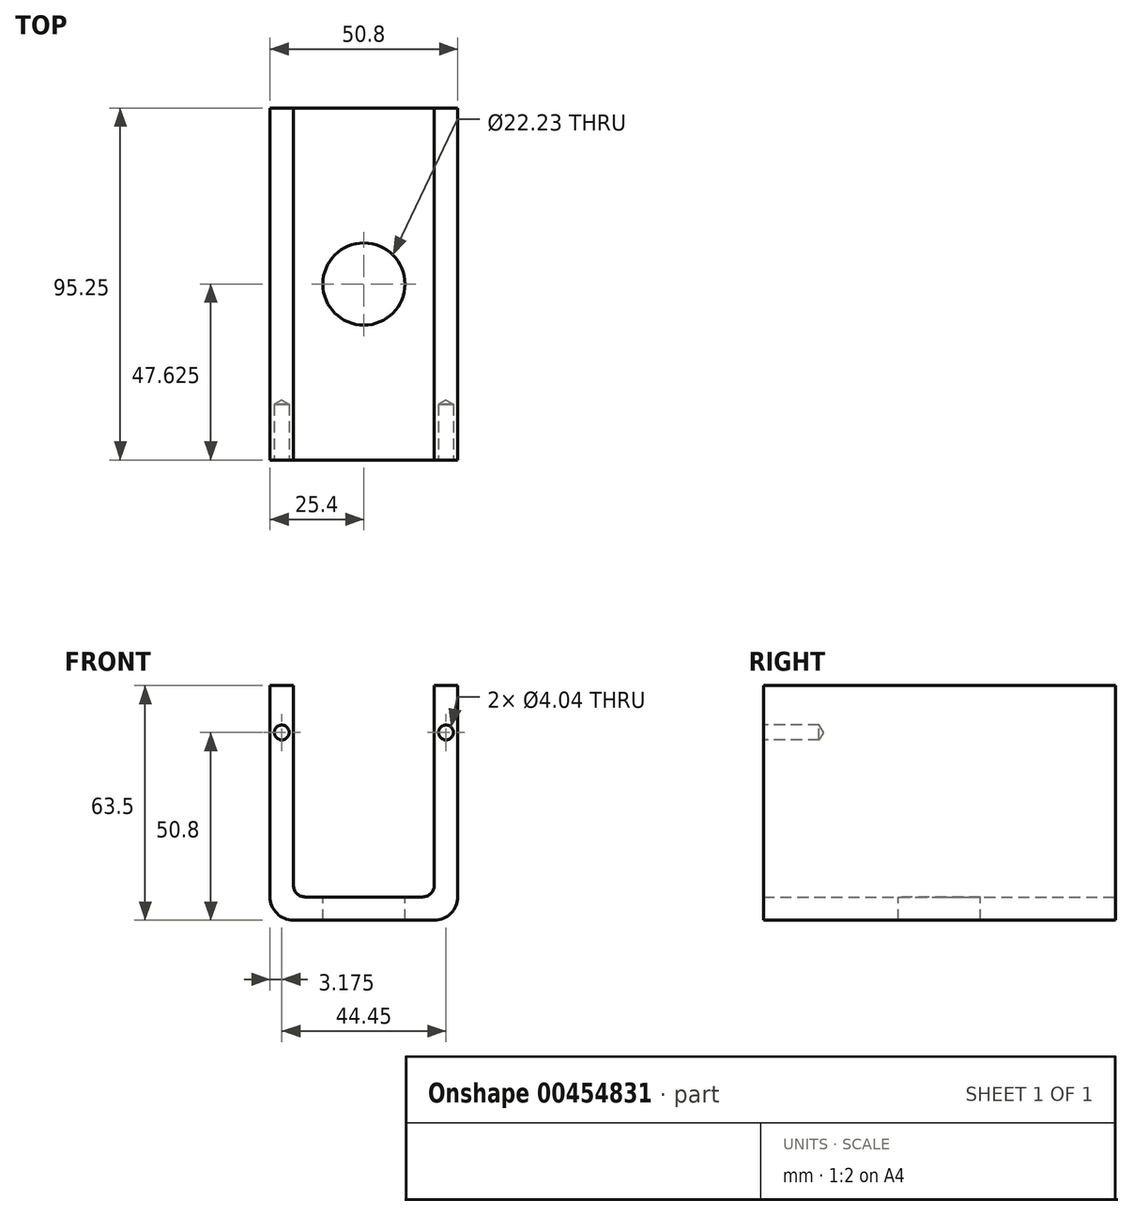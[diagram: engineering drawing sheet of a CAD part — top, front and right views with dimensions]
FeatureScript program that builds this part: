
annotation { "Feature Type Name" : "Feature", "Feature Type Description" : "" }
export const myFeature = defineFeature(function(context is Context, id is Id, definition is map)
    precondition{}
    {
        {
            var Q0;
            Q0=qCreatedBy(makeId("Front.planeOp"),FACE);
            var sketch = newSketch(context, id + "F0", { "sketchPlane" : qUnion([Q0])});
            skLineSegment(sketch, "E0", {"start": v(0, 0) * mm, "end": v(50.8, 0) * mm});
            skLineSegment(sketch, "E1", {"start": v(50.8, 0) * mm, "end": v(50.8, 63.5) * mm});
            skLineSegment(sketch, "E2", {"start": v(50.8, 63.5) * mm, "end": v(44.45, 63.5) * mm});
            skLineSegment(sketch, "E3", {"start": v(44.45, 63.5) * mm, "end": v(44.45, 6.29) * mm});
            skLineSegment(sketch, "E4", {"start": v(44.45, 6.29) * mm, "end": v(6.35, 6.29) * mm});
            skLineSegment(sketch, "E5", {"start": v(6.35, 6.29) * mm, "end": v(6.35, 63.5) * mm});
            skLineSegment(sketch, "E6", {"start": v(6.35, 63.5) * mm, "end": v(0, 63.5) * mm});
            skLineSegment(sketch, "E7", {"start": v(0, 63.5) * mm, "end": v(0, 0) * mm});
            skSolve(sketch);
        }
        {
            var Q0;
            Q0 = qSketchRegion(id + "F0", true);
            extrude(context, id + "F1", {"entities" : qUnion([Q0]), "depth" : 95.25 * mm});
        }
        {
            var Q0;
            Q0=makeQuery(id+"F1.opExtrude","SWEPT_EDGE",EDGE,{"disambiguationData":[OSD([sQuery(id+"F0.wireOp",EDGE,"E0"),sQuery(id+"F0.wireOp",EDGE,"E1")])]});
            var Q1;
            Q1=makeQuery(id+"F1.opExtrude","SWEPT_EDGE",EDGE,{"disambiguationData":[OSD([sQuery(id+"F0.wireOp",EDGE,"E0"),sQuery(id+"F0.wireOp",EDGE,"E7")])]});
            fillet(context, id + "F2", {"entities" : qUnion([Q0, Q1]), "radius" : 6.35 * mm, "tangentPropagation" : true, "allowEdgeOverflow" : false});
        }
        {
            var Q0;
            Q0=makeQuery(id+"F1.opExtrude","SWEPT_EDGE",EDGE,{"disambiguationData":[OSD([sQuery(id+"F0.wireOp",EDGE,"E3"),sQuery(id+"F0.wireOp",EDGE,"E4")])]});
            var Q1;
            Q1=makeQuery(id+"F1.opExtrude","SWEPT_EDGE",EDGE,{"disambiguationData":[OSD([sQuery(id+"F0.wireOp",EDGE,"E4"),sQuery(id+"F0.wireOp",EDGE,"E5")])]});
            fillet(context, id + "F3", {"entities" : qUnion([Q0, Q1]), "radius" : 3.17 * mm, "tangentPropagation" : true, "allowEdgeOverflow" : false});
        }
        {
            var Q0;
            Q0=makeQuery(id+"F1.opExtrude","CAP_FACE",FACE,{"disambiguationData":[OSD([sQuery(id+"F0.wireOp",EDGE,"E0"),sQuery(id+"F0.wireOp",EDGE,"E1"),sQuery(id+"F0.wireOp",EDGE,"E2"),sQuery(id+"F0.wireOp",EDGE,"E3"),sQuery(id+"F0.wireOp",EDGE,"E4"),sQuery(id+"F0.wireOp",EDGE,"E5"),sQuery(id+"F0.wireOp",EDGE,"E6"),sQuery(id+"F0.wireOp",EDGE,"E7")])],"isStart":false});
            var sketch = newSketch(context, id + "F4", { "sketchPlane" : qUnion([Q0])});
            skPoint(sketch, "E8", {"position": v(3.18, 50.8) * mm});
            skPoint(sketch, "E9", {"position": v(47.63, 50.8) * mm});
            skSolve(sketch);
        }
        {
            var Q0;
            Q0=sQuery(id+"F4.wireOp",VERTEX,"E8");
            var Q1;
            Q1=sQuery(id+"F4.wireOp",VERTEX,"E9");
            var Q2;
            Q2=makeQuery(id+"F1.opExtrude","SWEPT_BODY",BODY,{"disambiguationData":[OSD([sQuery(id+"F0.wireOp",EDGE,"E0"),sQuery(id+"F0.wireOp",EDGE,"E1"),sQuery(id+"F0.wireOp",EDGE,"E2"),sQuery(id+"F0.wireOp",EDGE,"E3"),sQuery(id+"F0.wireOp",EDGE,"E4"),sQuery(id+"F0.wireOp",EDGE,"E5"),sQuery(id+"F0.wireOp",EDGE,"E6"),sQuery(id+"F0.wireOp",EDGE,"E7")])]});
            hole(context, id + "F5", {"style" : HoleStyle.SIMPLE, "endStyle" : HoleEndStyle.BLIND, "standardTappedOrClearance" : lookupTablePath({ "standard" : "ANSI", "engagement" : "75%", "pitch" : "32 tpi", "size" : "#10", "type" : "Tapped" }), "standardBlindInLast" : lookupTablePath({ "standard" : "ANSI", "engagement" : "75%", "pitch" : "32 tpi", "size" : "#10", "type" : "Tapped" }), "holeDiameter" : 4.04 * mm, "showTappedDepth" : true, "holeDepth" : 15.08 * mm, "tappedDepth" : 12.7 * mm, "tapClearance" : 3, "startFromSketch" : true, "locations" : qUnion([Q0, Q1]), "scope" : qUnion([Q2]), "majorDiameter" : 4.83 * mm});
        }
        {
            var Q0;
            Q0=makeQuery(id+"F1.opExtrude","SWEPT_FACE",FACE,{"disambiguationData":[OSD([sQuery(id+"F0.wireOp",EDGE,"E4")])]});
            var sketch = newSketch(context, id + "F6", { "sketchPlane" : qUnion([Q0])});
            skCircle(sketch, "E10", {"center": v(25.4, -47.63) * mm, "radius": 11.11 * mm});
            skSolve(sketch);
        }
        {
            var Q0;
            Q0=sQuery(id+"F6.wireOp",VERTEX,"E10.center");
            var Q1;
            Q1=makeQuery(id+"F1.opExtrude","SWEPT_BODY",BODY,{"disambiguationData":[OSD([sQuery(id+"F0.wireOp",EDGE,"E0"),sQuery(id+"F0.wireOp",EDGE,"E1"),sQuery(id+"F0.wireOp",EDGE,"E2"),sQuery(id+"F0.wireOp",EDGE,"E3"),sQuery(id+"F0.wireOp",EDGE,"E4"),sQuery(id+"F0.wireOp",EDGE,"E5"),sQuery(id+"F0.wireOp",EDGE,"E6"),sQuery(id+"F0.wireOp",EDGE,"E7")])]});
            hole(context, id + "F7", {"style" : HoleStyle.SIMPLE, "endStyle" : HoleEndStyle.THROUGH, "holeDiameter" : 22.22 * mm, "tappedDepth" : 12.7 * mm, "tapClearance" : 3, "startFromSketch" : true, "locations" : qUnion([Q0]), "scope" : qUnion([Q1])});
        }
    });
